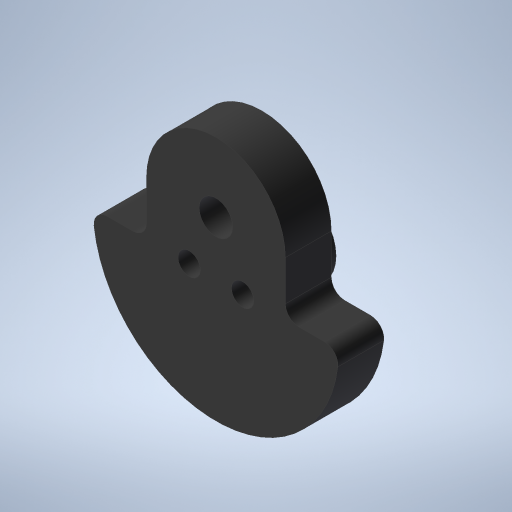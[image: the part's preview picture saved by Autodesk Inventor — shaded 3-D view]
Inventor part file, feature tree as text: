
AUTODESK INVENTOR PART (.ipt)
format: ipt  version: 2023 (Build 270158000, 158)  size: 479,744 bytes
history: native  units: in
note: dims shown in document units (in); Inventor stores cm internally (conversion verified against a paired STEP export)
features: extrude x5, sketch x1, fillet x1
ambient origin geometry x8: Origin, YZ Plane, XZ Plane, XY Plane, X Axis, Y Axis, Z Axis, Center Point
bodies: Body1 (feature_tree)
feature tree (7):
  sketch  "Sketch1"  dims[d3=0.866in d15=0.75in d20=0.314in d37=0.75in d44=0.125in d51=0.21in d52=0.21in d57=0.74in d58=0.75in d59=0.0in d60=0.32in d61=0.0in d62=1.5in d63=0.0in d64=1.5in d65=0.0in d66=0.375in d67=0.0in d68=0.125in]
  extrude  "Extrusion9"  Depth=0.125in
  extrude  "Extrusion10"  Depth=0.125in
  extrude  "Extrusion11"  Depth=0.125in
  extrude  "Extrusion12"  Depth=0.125in
  extrude  "Extrusion13"  Depth=0.125in
  fillet  "Fillet2"  Radius=0.74in
